FCSTD DOCUMENT  (FreeCAD 0.20R26155 (Git))
Label: SWD_pogo_landing
License: All rights reserved
LicenseURL: http://en.wikipedia.org/wiki/All_rights_reserved
objects: Sketcher::SketchObject×2
note: 2 computed .brp shape members not serialized (recipe doc carries the construction recipe); baked Part::Feature solids carry a one-line shape summary decoded from their .brp

FEATURE [Sketcher::SketchObject] Sketch  label="Pads_TH_SMD"
  FullyConstrained = true
  sketch-geometry (10):
    g0: Circle CenterX=1.1 CenterY=2.2 CenterZ=0 NormalX=0 NormalY=0 NormalZ=1 AngleXU=0 Radius=0.5
    g1: Circle CenterX=-1.1 CenterY=2.2 CenterZ=0 NormalX=0 NormalY=0 NormalZ=1 AngleXU=0 Radius=0.5
    g2: Circle CenterX=-1.1 CenterY=0 CenterZ=0 NormalX=0 NormalY=0 NormalZ=1 AngleXU=0 Radius=0.5
    g3: Circle CenterX=1.1 CenterY=0 CenterZ=0 NormalX=0 NormalY=0 NormalZ=1 AngleXU=0 Radius=0.5
    g4: Circle CenterX=1.1 CenterY=-2.2 CenterZ=0 NormalX=0 NormalY=0 NormalZ=1 AngleXU=0 Radius=0.5
    g5: Circle CenterX=-1.1 CenterY=-2.2 CenterZ=0 NormalX=0 NormalY=0 NormalZ=1 AngleXU=0 Radius=0.5
    g6: LineSegment StartX=-1.1 StartY=2.2 StartZ=0 EndX=1.1 EndY=2.2 EndZ=0
    g7: LineSegment StartX=1.1 StartY=2.2 StartZ=0 EndX=1.1 EndY=-2.2 EndZ=0
    g8: LineSegment StartX=1.1 StartY=-2.2 StartZ=0 EndX=-1.1 EndY=-2.2 EndZ=0
    g9: LineSegment StartX=-1.1 StartY=-2.2 StartZ=0 EndX=-1.1 EndY=2.2 EndZ=0
  constraints (24):
    c: Coincident(g6,g7)
    c: Coincident(g7,g8)
    c: Coincident(g8,g9)
    c: Coincident(g9,g6)
    c: Horizontal(g8)
    c: Vertical(g9)
    c: Coincident(g6,g1)
    c: Coincident(g7,g4)
    c: Coincident(g8,g5)
    c: Coincident(g0,g6)
    c: PointOnObject(g3,g7)
    c: PointOnObject(g2,g9)
    c: DistanceX(g6,g6) = 2.2
    c: Equal(g1,g0)
    c: Equal(g0,g2)
    c: Equal(g2,g3)
    c: Equal(g3,g5)
    c: Equal(g5,g4)
    c: Radius(g1) = 0.5
    c: Symmetric(g0,g1,g-2)
    c: Symmetric(g4,g0,g-1)
    c: PointOnObject(g2,g-1)
    c: PointOnObject(g3,g-1)
    c: DistanceY(g7,g7) = 4.4
FEATURE [Sketcher::SketchObject] Sketch001  label="Edge_Cuts_0.15"
  ExternalGeometry = -> [Sketch]
  FullyConstrained = false
  sketch-geometry (9):
    g0: ArcOfCircle CenterX=0 CenterY=-3.85 CenterZ=0 NormalX=0 NormalY=0 NormalZ=1 AngleXU=0 Radius=0.9 StartAngle=2e-16 EndAngle=3.14159
    g1: ArcOfCircle CenterX=0 CenterY=-6.7 CenterZ=0 NormalX=0 NormalY=0 NormalZ=1 AngleXU=0 Radius=0.9 StartAngle=3.14159 EndAngle=6.28319
    g2: LineSegment StartX=-0.9 StartY=-3.85 StartZ=0 EndX=-0.9 EndY=-6.7 EndZ=0
    g3: LineSegment StartX=0.9 StartY=-6.7 StartZ=0 EndX=0.9 EndY=-3.85 EndZ=0
    g4: LineSegment StartX=-0.988138 StartY=-2.95 StartZ=0 EndX=0.871614 EndY=-2.95 EndZ=0
    g5: LineSegment StartX=3.00286 StartY=-3.23123 StartZ=0 EndX=4.60286 EndY=-3.23123 EndZ=0
    g6: LineSegment StartX=4.60286 StartY=-3.23123 StartZ=0 EndX=4.60286 EndY=-6.23123 EndZ=0
    g7: LineSegment StartX=4.60286 StartY=-6.23123 StartZ=0 EndX=3.00286 EndY=-6.23123 EndZ=0
    g8: LineSegment StartX=3.00286 StartY=-6.23123 StartZ=0 EndX=3.00286 EndY=-3.23123 EndZ=0
  constraints (21):
    c: Tangent(g0,g2) = -1.5708
    c: Tangent(g2,g1) = -1.5708
    c: Tangent(g1,g3) = -1.5708
    c: Tangent(g3,g0) = -1.5708
    c: Equal(g0,g1)
    c: PointOnObject(g0,g-2)
    c: PointOnObject(g1,g-2)
    c: DistanceX(g1,g1) = 1.8
    c: Horizontal(g4)
    c: Tangent(g4,g0)
    c: DistanceY(g1,g0) = 2.85
    c: Coincident(g5,g6)
    c: Coincident(g6,g7)
    c: Coincident(g7,g8)
    c: Coincident(g8,g5)
    c: Horizontal(g5)
    c: Horizontal(g7)
    c: Vertical(g6)
    c: Vertical(g8)
    c: DistanceX(g5,g5) = 1.6
    c: DistanceY(g6,g6) = 3
